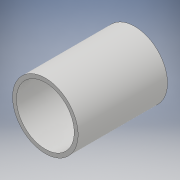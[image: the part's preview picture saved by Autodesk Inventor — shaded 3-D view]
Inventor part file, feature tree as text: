
AUTODESK INVENTOR PART (.ipt)
format: ipt  version: 2017 (Build 210142000, 142)  size: 97,280 bytes
history: native  units: mm
features: extrude x1, sketch x1
ambient origin geometry x8: Origin, YZ Plane, XZ Plane, XY Plane, X Axis, Y Axis, Z Axis, Center Point
bodies: Solid1 (feature_tree)
feature tree (2):
  extrude  "Extrusion1"  Depth=30.0mm
  sketch  "Sketch1"  dims[d0=22.0mm d1=1.3mm d2=30.0mm d3=0.0mm]
